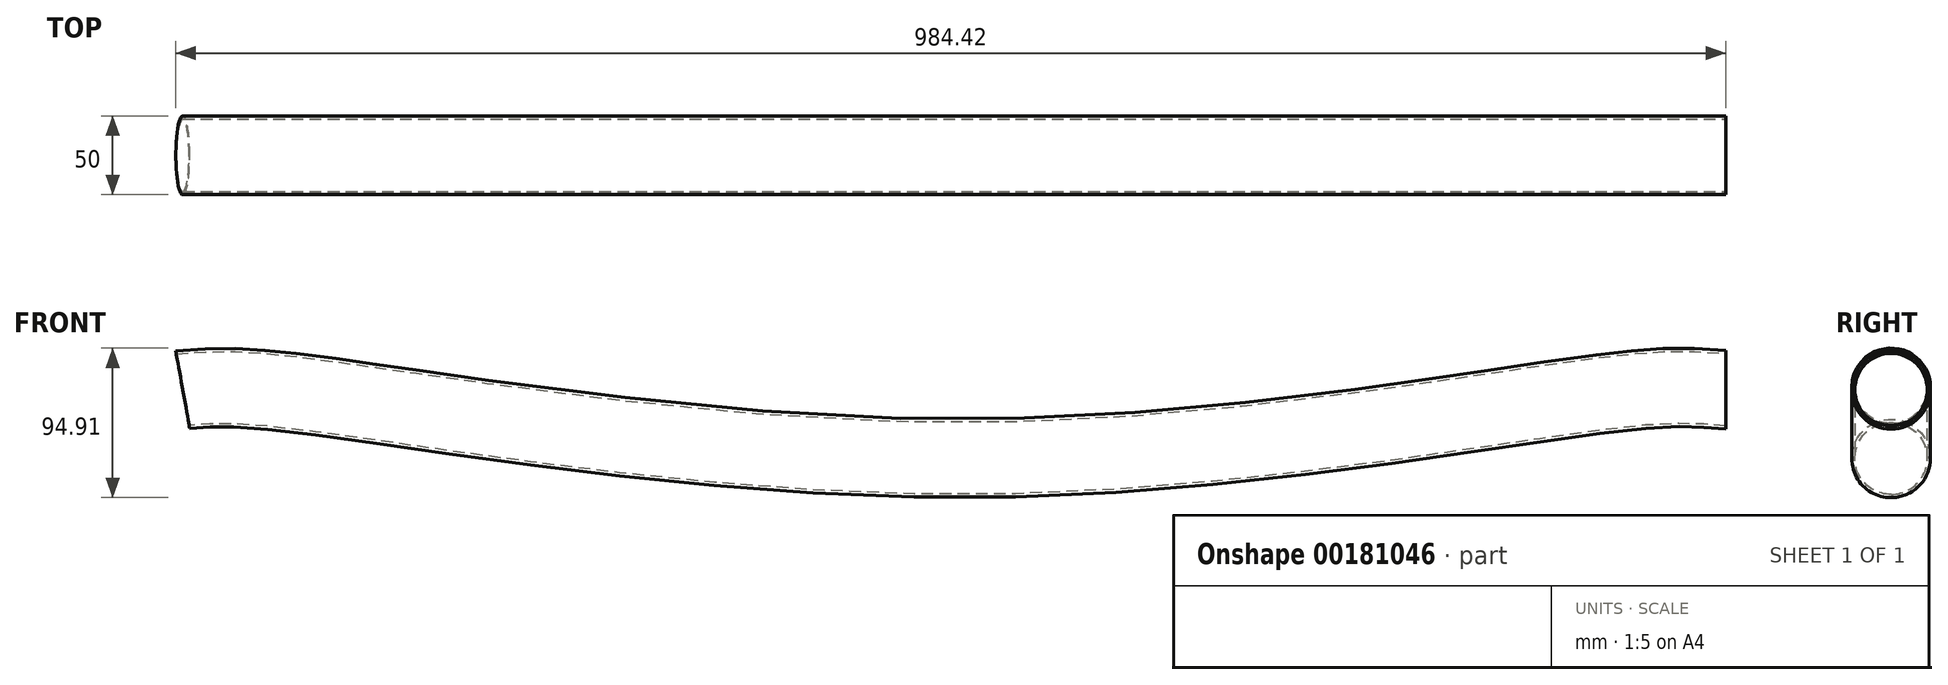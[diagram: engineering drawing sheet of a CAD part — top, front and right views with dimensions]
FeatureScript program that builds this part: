
annotation { "Feature Type Name" : "Feature", "Feature Type Description" : "" }
export const myFeature = defineFeature(function(context is Context, id is Id, definition is map)
    precondition{}
    {
        {
            var Q0;
            Q0=qCreatedBy(makeId("Front.planeOp"),FACE);
            var sketch = newSketch(context, id + "F0", { "sketchPlane" : qUnion([Q0])});
            skPoint(sketch, "E0", {"position": v(-495.98, 16.99) * mm});
            skPoint(sketch, "E1", {"position": v(484.02, 16.99) * mm});
            skFitSpline(sketch, "E2", {"points": [v(-495.98, 16.99) * mm, v(-443.65, 16.99) * mm, v(0, -26.63) * mm, v(427.66, 16.99) * mm, v(484.02, 16.99) * mm], "startDerivative": vector(308.3, 27.68) * mm, "endDerivative": vector(327.75, -28.88) * mm});
            skSolve(sketch);
        }
        {
            var Q0;
            Q0=sQuery(id+"F0.wireOp",VERTEX,"E1");
            var Q1;
            Q1=qCreatedBy(makeId("Right.planeOp"),FACE);
            cPlane(context, id + "F1", {"entities" : qUnion([Q0, Q1]), "cplaneType" : CPlaneType.PLANE_POINT, "offset" : 25 * mm, "width" : 150 * mm, "height" : 150 * mm});
        }
        {
            var Q0;
            Q0=qCreatedBy(id+"F1.planeOp",FACE);
            var sketch = newSketch(context, id + "F2", { "sketchPlane" : qUnion([Q0])});
            skPoint(sketch, "E3.0", {"position": v(0, 16.99) * mm});
            skCircle(sketch, "E4", {"center": v(0, 16.99) * mm, "radius": 25 * mm});
            skCircle(sketch, "E5.0", {"center": v(0, 16.99) * mm, "radius": 23 * mm});
            skSolve(sketch);
        }
        {
            var Q0;
            Q0=makeQuery(id+"F2.imprint","IMPRINT",FACE,{"disambiguationData":[TD([[makeQuery(id+"F2.imprint","IMPRINT",EDGE,{"derivedFrom":sQuery(id+"F2.wireOp",EDGE,"E4")}),1.0]])]});
            var Q1;
            Q1=sQuery(id+"F0.wireOp",EDGE,"E2");
            sweep(context, id + "F3", {"profiles" : qUnion([Q0]), "path" : qUnion([Q1])});
        }
    });
